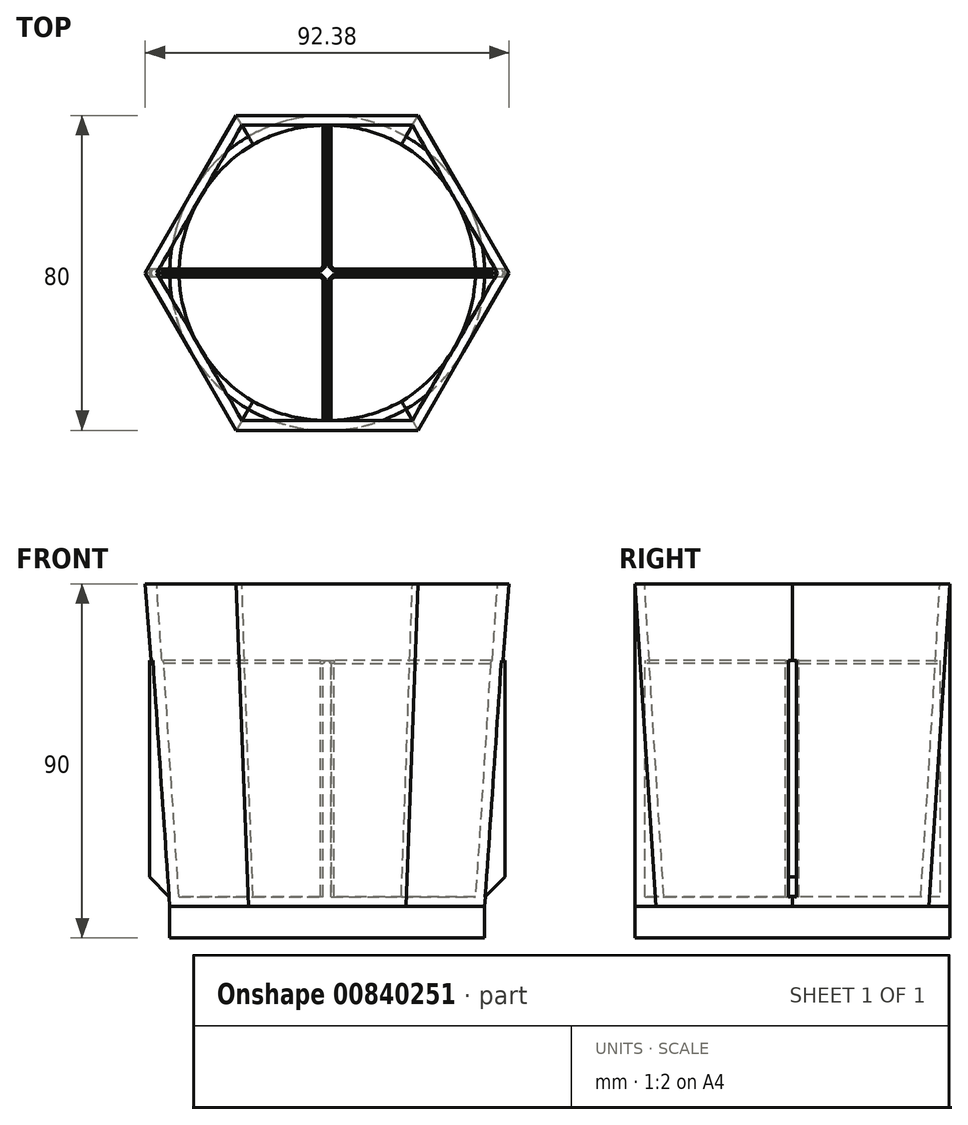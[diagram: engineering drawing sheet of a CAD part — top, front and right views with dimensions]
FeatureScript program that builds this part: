
annotation { "Feature Type Name" : "Feature", "Feature Type Description" : "" }
export const myFeature = defineFeature(function(context is Context, id is Id, definition is map)
    precondition{}
    {
        {
            var Q0;
            Q0=qCreatedBy(makeId("Top.planeOp"),FACE);
            var sketch = newSketch(context, id + "F0", { "sketchPlane" : qUnion([Q0])});
            skCircle(sketch, "E0", {"center": v(0, 0) * mm, "radius": 40 * mm});
            skSolve(sketch);
        }
        {
            var Q0;
            Q0=qCreatedBy(makeId("Top.planeOp"),FACE);
            cPlane(context, id + "F1", {"entities" : qUnion([Q0]), "cplaneType" : CPlaneType.OFFSET, "offset" : 90 * mm, "width" : 150 * mm, "height" : 150 * mm});
        }
        {
            var Q0;
            Q0=qCreatedBy(id+"F1.planeOp",FACE);
            var sketch = newSketch(context, id + "F2", { "sketchPlane" : qUnion([Q0])});
            skCircle(sketch, "E1.cCircle", {"center": v(0, 0) * mm, "radius": 40 * mm, "construction": true});
            skLineSegment(sketch, "E1.0", {"start": v(-23.1, 40) * mm, "end": v(23.1, 40) * mm});
            skLineSegment(sketch, "E1.1", {"start": v(23.1, 40) * mm, "end": v(46.19, 0) * mm});
            skLineSegment(sketch, "E1.2", {"start": v(46.19, 0) * mm, "end": v(23.1, -40) * mm});
            skLineSegment(sketch, "E1.3", {"start": v(23.1, -40) * mm, "end": v(-23.1, -40) * mm});
            skLineSegment(sketch, "E1.4", {"start": v(-23.1, -40) * mm, "end": v(-46.19, 0) * mm});
            skLineSegment(sketch, "E1.5", {"start": v(-46.19, 0) * mm, "end": v(-23.1, 40) * mm});
            skPoint(sketch, "E1.0.midPoint", {"position": v(0, 40) * mm});
            skSolve(sketch);
        }
        {
            var Q0;
            Q0=qSketchRegion(id+"F0",true);
            extrude(context, id + "F3", {"entities" : qUnion([Q0]), "depth" : 8 * mm, "offsetDistance" : 25 * mm});
        }
        {
            var Q0;
            Q0=makeQuery(id+"F3.opExtrude","CAP_FACE",FACE,{"disambiguationData":[OSD([sQuery(id+"F0.wireOp",EDGE,"E0")])],"isStart":false});
            var sketch = newSketch(context, id + "F4", { "sketchPlane" : qUnion([Q0])});
            skSolve(sketch);
        }
        {
            var Q0;
            Q0=makeQuery(id+"F4.imprint","IMPRINT",FACE,{"disambiguationData":[TD([[makeQuery(id+"F4.imprint","IMPRINT",EDGE,{"derivedFrom":makeQuery(id+"F3.opExtrude","CAP_EDGE",EDGE,{"disambiguationData":[OSD([sQuery(id+"F0.wireOp",EDGE,"E0")])],"isStart":false})}),1.0]])]});
            var Q1;
            Q1=makeQuery(id+"F2.imprint","IMPRINT",FACE,{"disambiguationData":[TD([[makeQuery(id+"F2.imprint","IMPRINT",EDGE,{"derivedFrom":sQuery(id+"F2.wireOp",EDGE,"E1.0")}),-1.0]])]});
            loft(context, id + "F5", {"sheetProfilesArray" : [{ "sheetProfileEntities" : qUnion([Q0]) }, { "sheetProfileEntities" : qUnion([Q1]) }]});
        }
        {
            var Q0;
            Q0=makeQuery(id+"F5.opLoft","CAP_FACE",FACE,{"disambiguationData":[OSD([makeQuery(id+"F2.imprint","IMPRINT",FACE,{"disambiguationData":[TD([[makeQuery(id+"F2.imprint","IMPRINT",EDGE,{"derivedFrom":sQuery(id+"F2.wireOp",EDGE,"E1.0")}),-1.0]])]})])],"isStart":true});
            shell(context, id + "F6", {"entities" : qUnion([Q0]), "thickness" : 2.5 * mm});
        }
        {
            var Q0;
            Q0=makeQuery(id+"F6.opShell","OFFSET_FACE",FACE,{"disambiguationData":[OSD([makeQuery(id+"F4.imprint","IMPRINT",FACE,{"disambiguationData":[TD([[makeQuery(id+"F4.imprint","IMPRINT",EDGE,{"derivedFrom":makeQuery(id+"F3.opExtrude","CAP_EDGE",EDGE,{"disambiguationData":[OSD([sQuery(id+"F0.wireOp",EDGE,"E0")])],"isStart":false})}),1.0]])]})])]});
            var sketch = newSketch(context, id + "F7", { "sketchPlane" : qUnion([Q0])});
            skLineSegment(sketch, "E2.bottom", {"start": v(-1, 39.83) * mm, "end": v(1, 39.83) * mm});
            skLineSegment(sketch, "E2.top", {"start": v(-1, -39.83) * mm, "end": v(1, -39.83) * mm});
            skLineSegment(sketch, "E2.left", {"start": v(-1, 39.83) * mm, "end": v(-1, -39.83) * mm});
            skLineSegment(sketch, "E2.right", {"start": v(1, 39.83) * mm, "end": v(1, -39.83) * mm});
            skPoint(sketch, "E2.middle", {"position": v(0, 0) * mm});
            skLineSegment(sketch, "E3.bottom", {"start": v(45.15, 1) * mm, "end": v(-45.15, 1) * mm});
            skLineSegment(sketch, "E3.top", {"start": v(45.15, -1) * mm, "end": v(-45.15, -1) * mm});
            skLineSegment(sketch, "E3.left", {"start": v(45.15, 1) * mm, "end": v(45.15, -1) * mm});
            skLineSegment(sketch, "E3.right", {"start": v(-45.15, 1) * mm, "end": v(-45.15, -1) * mm});
            skSolve(sketch);
        }
        {
            var Q0;
            Q0=qSketchRegion(id+"F7",true);
            extrude(context, id + "F8", {"entities" : qUnion([Q0]), "operationType" : NewBodyOperationType.ADD, "depth" : 60 * mm, "offsetDistance" : 25 * mm});
        }
        {
            var Q0;
            {var subQ0=sQuery(id+"F2.wireOp",EDGE,"E1.5");var subQ1=sQuery(id+"F2.wireOp",EDGE,"E1.0");var subQ2=sQuery(id+"F0.wireOp",EDGE,"E0");var subQ3=sQuery(id+"F7.wireOp",EDGE,"E3.bottom");var subQ4=sQuery(id+"F7.wireOp",EDGE,"E2.left");var subQ5=makeQuery(id+"F7.imprint","INTERSECT",VERTEX,{"derivedFrom":[subQ4,subQ3]});var subQ8=sQuery(id+"F7.wireOp",EDGE,"E3.right");var subQ10=makeQuery(id+"F7.imprint","IMPRINT",EDGE,{"disambiguationData":[TD([[makeQuery(id+"F7.imprint","INTERSECT",VERTEX,{"derivedFrom":[subQ3,subQ8]}),1.0]])],"derivedFrom":subQ3});var subQ11=makeQuery(id+"F7.imprint","IMPRINT",EDGE,{"disambiguationData":[TD([[subQ5,-1.0]])],"derivedFrom":subQ3});Q0=makeQuery(id+"F8.boolean.opBoolean","SPLIT",EDGE,{"disambiguationData":[TD([makeQuery(id+"F6.opShell","OFFSET_FACE",FACE,{"disambiguationData":[OSD([subQ2,subQ1,sQuery(id+"F2.wireOp",EDGE,"E1.4"),subQ0])]})])],"derivedFrom":makeQuery(id+"F8.opExtrude","CAP_EDGE",EDGE,{"disambiguationData":[OSD([subQ3]),TDD([subQ11,subQ10])],"isStart":false})});}
            var Q1;
            {var subQ0=sQuery(id+"F2.wireOp",EDGE,"E1.5");var subQ1=sQuery(id+"F2.wireOp",EDGE,"E1.4");var subQ2=sQuery(id+"F2.wireOp",EDGE,"E1.3");var subQ3=sQuery(id+"F2.wireOp",EDGE,"E1.0");var subQ4=sQuery(id+"F0.wireOp",EDGE,"E0");var subQ5=sQuery(id+"F7.wireOp",EDGE,"E3.right");var subQ6=sQuery(id+"F7.wireOp",EDGE,"E3.top");var subQ7=sQuery(id+"F7.wireOp",EDGE,"E2.left");var subQ10=makeQuery(id+"F7.imprint","INTERSECT",VERTEX,{"derivedFrom":[subQ7,subQ6]});var subQ12=makeQuery(id+"F7.imprint","IMPRINT",EDGE,{"disambiguationData":[TD([[makeQuery(id+"F7.imprint","INTERSECT",VERTEX,{"derivedFrom":[subQ6,subQ5]}),1.0]])],"derivedFrom":subQ6});var subQ13=makeQuery(id+"F7.imprint","IMPRINT",EDGE,{"disambiguationData":[TD([[subQ10,-1.0]])],"derivedFrom":subQ6});Q1=makeQuery(id+"F8.boolean.opBoolean","SPLIT",EDGE,{"disambiguationData":[TD([makeQuery(id+"F6.opShell","OFFSET_FACE",FACE,{"disambiguationData":[OSD([subQ4,subQ3,subQ2,subQ1,subQ0])]})])],"derivedFrom":makeQuery(id+"F8.opExtrude","CAP_EDGE",EDGE,{"disambiguationData":[OSD([subQ6]),TDD([subQ13,subQ12])],"isStart":false})});}
            var Q2;
            {var subQ5=sQuery(id+"F7.wireOp",EDGE,"E3.right");var subQ6=sQuery(id+"F7.wireOp",EDGE,"E3.bottom");var subQ7=sQuery(id+"F7.wireOp",EDGE,"E2.left");var subQ8=sQuery(id+"F7.wireOp",EDGE,"E2.bottom");var subQ9=makeQuery(id+"F7.imprint","INTERSECT",VERTEX,{"derivedFrom":[subQ7,subQ6]});var subQ11=makeQuery(id+"F7.imprint","IMPRINT",EDGE,{"disambiguationData":[TD([[subQ9,1.0]])],"derivedFrom":subQ7});var subQ12=makeQuery(id+"F7.imprint","IMPRINT",EDGE,{"disambiguationData":[TD([[makeQuery(id+"F7.imprint","INTERSECT",VERTEX,{"derivedFrom":[subQ8,subQ7]}),-1.0]])],"derivedFrom":subQ7});Q2=makeQuery(id+"F8.boolean.opBoolean","SPLIT",EDGE,{"disambiguationData":[TD([makeQuery(id+"F8.opExtrude","SWEPT_FACE",FACE,{"disambiguationData":[OSD([subQ6]),TDD([makeQuery(id+"F7.imprint","IMPRINT",EDGE,{"disambiguationData":[TD([[subQ9,-1.0]])],"derivedFrom":subQ6}),makeQuery(id+"F7.imprint","IMPRINT",EDGE,{"disambiguationData":[TD([[makeQuery(id+"F7.imprint","INTERSECT",VERTEX,{"derivedFrom":[subQ6,subQ5]}),1.0]])],"derivedFrom":subQ6})])]})])],"derivedFrom":makeQuery(id+"F8.opExtrude","CAP_EDGE",EDGE,{"disambiguationData":[OSD([subQ7]),TDD([subQ12,subQ11])],"isStart":false})});}
            var Q3;
            {var subQ0=sQuery(id+"F2.wireOp",EDGE,"E1.5");var subQ1=sQuery(id+"F2.wireOp",EDGE,"E1.2");var subQ2=sQuery(id+"F2.wireOp",EDGE,"E1.1");var subQ3=sQuery(id+"F2.wireOp",EDGE,"E1.0");var subQ4=sQuery(id+"F0.wireOp",EDGE,"E0");var subQ6=sQuery(id+"F7.wireOp",EDGE,"E3.bottom");var subQ7=sQuery(id+"F7.wireOp",EDGE,"E2.right");var subQ8=sQuery(id+"F7.wireOp",EDGE,"E2.bottom");var subQ9=makeQuery(id+"F7.imprint","INTERSECT",VERTEX,{"derivedFrom":[subQ7,subQ6]});var subQ11=makeQuery(id+"F7.imprint","IMPRINT",EDGE,{"disambiguationData":[TD([[subQ9,1.0]])],"derivedFrom":subQ7});var subQ12=makeQuery(id+"F7.imprint","IMPRINT",EDGE,{"disambiguationData":[TD([[makeQuery(id+"F7.imprint","INTERSECT",VERTEX,{"derivedFrom":[subQ8,subQ7]}),-1.0]])],"derivedFrom":subQ7});Q3=makeQuery(id+"F8.boolean.opBoolean","SPLIT",EDGE,{"disambiguationData":[TD([makeQuery(id+"F6.opShell","OFFSET_FACE",FACE,{"disambiguationData":[OSD([subQ4,subQ3,subQ2,subQ1,subQ0])]})])],"derivedFrom":makeQuery(id+"F8.opExtrude","CAP_EDGE",EDGE,{"disambiguationData":[OSD([subQ7]),TDD([subQ12,subQ11])],"isStart":false})});}
            var Q4;
            {var subQ0=sQuery(id+"F2.wireOp",EDGE,"E1.4");var subQ1=sQuery(id+"F2.wireOp",EDGE,"E1.3");var subQ2=sQuery(id+"F2.wireOp",EDGE,"E1.2");var subQ3=sQuery(id+"F0.wireOp",EDGE,"E0");var subQ4=sQuery(id+"F7.wireOp",EDGE,"E3.left");var subQ5=sQuery(id+"F7.wireOp",EDGE,"E3.top");var subQ6=sQuery(id+"F7.wireOp",EDGE,"E2.right");var subQ10=makeQuery(id+"F7.imprint","INTERSECT",VERTEX,{"derivedFrom":[subQ6,subQ5]});var subQ12=makeQuery(id+"F7.imprint","IMPRINT",EDGE,{"disambiguationData":[TD([[subQ10,1.0]])],"derivedFrom":subQ5});var subQ13=makeQuery(id+"F7.imprint","IMPRINT",EDGE,{"disambiguationData":[TD([[makeQuery(id+"F7.imprint","INTERSECT",VERTEX,{"derivedFrom":[subQ5,subQ4]}),-1.0]])],"derivedFrom":subQ5});Q4=makeQuery(id+"F8.boolean.opBoolean","SPLIT",EDGE,{"disambiguationData":[TD([makeQuery(id+"F6.opShell","OFFSET_FACE",FACE,{"disambiguationData":[OSD([subQ3,sQuery(id+"F2.wireOp",EDGE,"E1.1"),subQ2,subQ1,subQ0])]})])],"derivedFrom":makeQuery(id+"F8.opExtrude","CAP_EDGE",EDGE,{"disambiguationData":[OSD([subQ5]),TDD([subQ13,subQ12])],"isStart":false})});}
            var Q5;
            {var subQ0=sQuery(id+"F2.wireOp",EDGE,"E1.5");var subQ1=sQuery(id+"F2.wireOp",EDGE,"E1.4");var subQ2=sQuery(id+"F2.wireOp",EDGE,"E1.3");var subQ3=sQuery(id+"F2.wireOp",EDGE,"E1.2");var subQ4=sQuery(id+"F0.wireOp",EDGE,"E0");var subQ6=sQuery(id+"F7.wireOp",EDGE,"E3.top");var subQ7=sQuery(id+"F7.wireOp",EDGE,"E2.right");var subQ8=sQuery(id+"F7.wireOp",EDGE,"E2.top");var subQ10=makeQuery(id+"F7.imprint","IMPRINT",EDGE,{"disambiguationData":[TD([[makeQuery(id+"F7.imprint","INTERSECT",VERTEX,{"derivedFrom":[subQ8,subQ7]}),1.0]])],"derivedFrom":subQ7});var subQ11=makeQuery(id+"F7.imprint","INTERSECT",VERTEX,{"derivedFrom":[subQ7,subQ6]});var subQ12=makeQuery(id+"F7.imprint","IMPRINT",EDGE,{"disambiguationData":[TD([[subQ11,-1.0]])],"derivedFrom":subQ7});Q5=makeQuery(id+"F8.boolean.opBoolean","SPLIT",EDGE,{"disambiguationData":[TD([makeQuery(id+"F6.opShell","OFFSET_FACE",FACE,{"disambiguationData":[OSD([subQ4,subQ3,subQ2,subQ1,subQ0])]})])],"derivedFrom":makeQuery(id+"F8.opExtrude","CAP_EDGE",EDGE,{"disambiguationData":[OSD([subQ7]),TDD([subQ12,subQ10])],"isStart":false})});}
            var Q6;
            {var subQ0=sQuery(id+"F2.wireOp",EDGE,"E1.5");var subQ1=sQuery(id+"F2.wireOp",EDGE,"E1.4");var subQ2=sQuery(id+"F2.wireOp",EDGE,"E1.3");var subQ3=sQuery(id+"F0.wireOp",EDGE,"E0");var subQ5=sQuery(id+"F7.wireOp",EDGE,"E3.top");var subQ6=sQuery(id+"F7.wireOp",EDGE,"E2.left");var subQ7=sQuery(id+"F7.wireOp",EDGE,"E2.top");var subQ9=makeQuery(id+"F7.imprint","IMPRINT",EDGE,{"disambiguationData":[TD([[makeQuery(id+"F7.imprint","INTERSECT",VERTEX,{"derivedFrom":[subQ7,subQ6]}),1.0]])],"derivedFrom":subQ6});var subQ10=makeQuery(id+"F7.imprint","INTERSECT",VERTEX,{"derivedFrom":[subQ6,subQ5]});var subQ11=makeQuery(id+"F7.imprint","IMPRINT",EDGE,{"disambiguationData":[TD([[subQ10,-1.0]])],"derivedFrom":subQ6});Q6=makeQuery(id+"F8.boolean.opBoolean","SPLIT",EDGE,{"disambiguationData":[TD([makeQuery(id+"F6.opShell","OFFSET_FACE",FACE,{"disambiguationData":[OSD([subQ3,sQuery(id+"F2.wireOp",EDGE,"E1.2"),subQ2,subQ1,subQ0])]})])],"derivedFrom":makeQuery(id+"F8.opExtrude","CAP_EDGE",EDGE,{"disambiguationData":[OSD([subQ6]),TDD([subQ11,subQ9])],"isStart":false})});}
            var Q7;
            Q7=makeQuery(id+"F8.opExtrude","SWEPT_EDGE",EDGE,{"disambiguationData":[OSD([sQuery(id+"F7.wireOp",EDGE,"E2.right"),sQuery(id+"F7.wireOp",EDGE,"E3.top")])]});
            var Q8;
            Q8=makeQuery(id+"F8.opExtrude","SWEPT_EDGE",EDGE,{"disambiguationData":[OSD([sQuery(id+"F7.wireOp",EDGE,"E2.right"),sQuery(id+"F7.wireOp",EDGE,"E3.bottom")])]});
            var Q9;
            Q9=makeQuery(id+"F8.opExtrude","SWEPT_EDGE",EDGE,{"disambiguationData":[OSD([sQuery(id+"F7.wireOp",EDGE,"E2.left"),sQuery(id+"F7.wireOp",EDGE,"E3.bottom")])]});
            var Q10;
            Q10=makeQuery(id+"F8.opExtrude","SWEPT_EDGE",EDGE,{"disambiguationData":[OSD([sQuery(id+"F7.wireOp",EDGE,"E2.left"),sQuery(id+"F7.wireOp",EDGE,"E3.top")])]});
            chamfer(context, id + "F9", {"entities" : qUnion([Q0, Q1, Q2, Q3, Q4, Q5, Q6, Q7, Q8, Q9, Q10]), "width" : 0.7 * mm, "tangentPropagation" : true});
        }
        {
            var Q0;
            Q0=makeQuery(id+"F8.opExtrude","CAP_EDGE",EDGE,{"disambiguationData":[OSD([sQuery(id+"F7.wireOp",EDGE,"E3.right")])],"isStart":true});
            var Q1;
            Q1=makeQuery(id+"F8.opExtrude","CAP_EDGE",EDGE,{"disambiguationData":[OSD([sQuery(id+"F7.wireOp",EDGE,"E3.left")])],"isStart":true});
            chamfer(context, id + "F10", {"entities" : qUnion([Q0, Q1]), "width" : 5 * mm, "tangentPropagation" : true});
        }
    });
